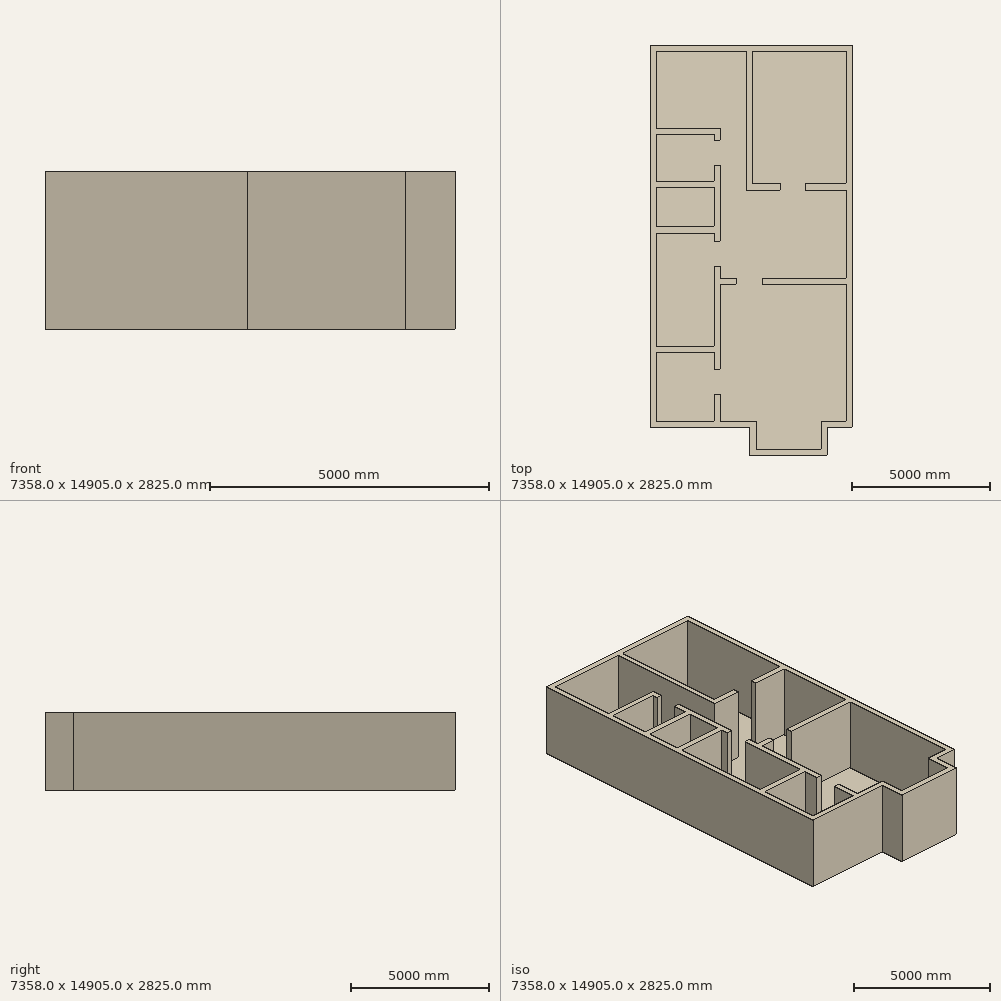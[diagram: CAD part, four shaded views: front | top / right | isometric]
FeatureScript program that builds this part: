
annotation { "Feature Type Name" : "Feature", "Feature Type Description" : "" }
export const myFeature = defineFeature(function(context is Context, id is Id, definition is map)
    precondition{}
    {
        {
            var Q0;
            Q0=qCreatedBy(makeId("Top.planeOp"),FACE);
            var sketch = newSketch(context, id + "F0", { "sketchPlane" : qUnion([Q0])});
            skLineSegment(sketch, "E0.bottom", {"start": v(0, 0) * mm, "end": v(2089, 0) * mm});
            skLineSegment(sketch, "E0.top", {"start": v(0, 13440) * mm, "end": v(3275, 13440) * mm});
            skLineSegment(sketch, "E0.left", {"start": v(0, 0) * mm, "end": v(0, 1938.71) * mm});
            skLineSegment(sketch, "E0.right", {"start": v(6900, 0) * mm, "end": v(6900, 4974) * mm});
            skLineSegment(sketch, "E1.0", {"start": v(7129, -229) * mm, "end": v(7129, 13669) * mm});
            skLineSegment(sketch, "E1.1", {"start": v(-229, -229) * mm, "end": v(3391, -229) * mm});
            skLineSegment(sketch, "E1.2", {"start": v(-229, -229) * mm, "end": v(-229, 13669) * mm});
            skLineSegment(sketch, "E1.3", {"start": v(-229, 13669) * mm, "end": v(7129, 13669) * mm});
            skLineSegment(sketch, "E2", {"start": v(6900, 4974) * mm, "end": v(3832.25, 4974) * mm});
            skLineSegment(sketch, "E3", {"start": v(3832.25, 4974) * mm, "end": v(3832.25, 5203) * mm});
            skLineSegment(sketch, "E4", {"start": v(3832.25, 5203) * mm, "end": v(6900, 5203) * mm});
            skLineSegment(sketch, "E5.trimOffspring", {"start": v(6900, 5203) * mm, "end": v(6900, 13440) * mm});
            skLineSegment(sketch, "E6", {"start": v(2318, 1893.08) * mm, "end": v(2318, 5631) * mm});
            skLineSegment(sketch, "E7", {"start": v(0, 0) * mm, "end": v(0, 2512) * mm});
            skLineSegment(sketch, "E8", {"start": v(0, 10652) * mm, "end": v(2318, 10652) * mm});
            skLineSegment(sketch, "E9", {"start": v(2089, 10423) * mm, "end": v(0, 10423) * mm});
            skLineSegment(sketch, "E10", {"start": v(0, 8735) * mm, "end": v(2089, 8735) * mm});
            skLineSegment(sketch, "E11", {"start": v(0, 8506) * mm, "end": v(2089, 8506) * mm});
            skLineSegment(sketch, "E12", {"start": v(0, 7080) * mm, "end": v(2089, 7080) * mm});
            skLineSegment(sketch, "E13", {"start": v(0, 6851) * mm, "end": v(2089, 6851) * mm});
            skLineSegment(sketch, "E14", {"start": v(0, 2741) * mm, "end": v(2089, 2741) * mm});
            skLineSegment(sketch, "E15", {"start": v(0, 2512) * mm, "end": v(2089, 2512) * mm});
            skLineSegment(sketch, "E16", {"start": v(2318, 1893.08) * mm, "end": v(2089, 1893.08) * mm});
            skLineSegment(sketch, "E17", {"start": v(2089, 1893.08) * mm, "end": v(2089, 2512) * mm});
            skLineSegment(sketch, "E18.trimOffspring", {"start": v(0, 2741) * mm, "end": v(0, 6851) * mm});
            skLineSegment(sketch, "E19.trimOffspring", {"start": v(2089, 2741) * mm, "end": v(2089, 5631) * mm});
            skLineSegment(sketch, "E20.trimOffspring", {"start": v(2089, 7080) * mm, "end": v(2089, 8506) * mm});
            skLineSegment(sketch, "E21.trimOffspring", {"start": v(0, 7080) * mm, "end": v(0, 8506) * mm});
            skLineSegment(sketch, "E22.trimOffspring", {"start": v(2089, 8735) * mm, "end": v(2089, 9303) * mm});
            skLineSegment(sketch, "E23.trimOffspring", {"start": v(0, 8735) * mm, "end": v(0, 13440) * mm});
            skLineSegment(sketch, "E24", {"start": v(2089, 973.08) * mm, "end": v(2089, 0) * mm});
            skLineSegment(sketch, "E25", {"start": v(2089, 973.08) * mm, "end": v(2318, 973.08) * mm});
            skLineSegment(sketch, "E26", {"start": v(2318, 973.08) * mm, "end": v(2318, 0) * mm});
            skLineSegment(sketch, "E27.trimOffspring", {"start": v(2318, 0) * mm, "end": v(3620, 0) * mm});
            skLineSegment(sketch, "E28", {"start": v(2318, 5203) * mm, "end": v(2912.25, 5203) * mm});
            skLineSegment(sketch, "E29", {"start": v(2912.25, 5203) * mm, "end": v(2912.25, 4974) * mm});
            skLineSegment(sketch, "E30", {"start": v(2912.25, 4974) * mm, "end": v(2318, 4974) * mm});
            skLineSegment(sketch, "E31", {"start": v(2089, 6551) * mm, "end": v(2318, 6551) * mm});
            skLineSegment(sketch, "E32", {"start": v(2089, 5631) * mm, "end": v(2318, 5631) * mm});
            skLineSegment(sketch, "E33.trimOffspring", {"start": v(2089, 6551) * mm, "end": v(2089, 6851) * mm});
            skLineSegment(sketch, "E34.trimOffspring", {"start": v(2318, 6551) * mm, "end": v(2318, 9303) * mm});
            skLineSegment(sketch, "E35", {"start": v(2089, 10223) * mm, "end": v(2318, 10223) * mm});
            skLineSegment(sketch, "E36", {"start": v(2089, 9303) * mm, "end": v(2318, 9303) * mm});
            skLineSegment(sketch, "E37.trimOffspring", {"start": v(2318, 10223) * mm, "end": v(2318, 10652) * mm});
            skLineSegment(sketch, "E38.trimOffspring", {"start": v(2089, 10223) * mm, "end": v(2089, 10423) * mm});
            skPoint(sketch, "E39.endSnap0", {"position": v(3450, 13440) * mm});
            skLineSegment(sketch, "E40", {"start": v(6900, 8638) * mm, "end": v(5416.42, 8638) * mm});
            skLineSegment(sketch, "E41", {"start": v(5416.42, 8638) * mm, "end": v(5416.42, 8409) * mm});
            skLineSegment(sketch, "E42", {"start": v(5416.42, 8409) * mm, "end": v(6900, 8409) * mm});
            skLineSegment(sketch, "E43", {"start": v(3504, 13440) * mm, "end": v(3504, 8638) * mm});
            skLineSegment(sketch, "E44", {"start": v(3275, 13440) * mm, "end": v(3275, 8409) * mm});
            skLineSegment(sketch, "E45", {"start": v(3275, 8409) * mm, "end": v(4496.42, 8409) * mm});
            skLineSegment(sketch, "E46", {"start": v(4496.42, 8409) * mm, "end": v(4496.42, 8638) * mm});
            skLineSegment(sketch, "E47", {"start": v(4496.42, 8638) * mm, "end": v(3504, 8638) * mm});
            skLineSegment(sketch, "E48.trimOffspring", {"start": v(3504, 13440) * mm, "end": v(6900, 13440) * mm});
            skLineSegment(sketch, "E49", {"start": v(6229, -229) * mm, "end": v(6229, -1236) * mm});
            skLineSegment(sketch, "E50", {"start": v(6229, -1236) * mm, "end": v(3391, -1236) * mm});
            skLineSegment(sketch, "E51", {"start": v(3391, -1236) * mm, "end": v(3391, -229) * mm});
            skLineSegment(sketch, "E52", {"start": v(3620, 0) * mm, "end": v(3620, -1007) * mm});
            skLineSegment(sketch, "E53", {"start": v(3620, -1007) * mm, "end": v(6000, -1007) * mm});
            skLineSegment(sketch, "E54", {"start": v(6000, -1007) * mm, "end": v(6000, 0) * mm});
            skLineSegment(sketch, "E55.trimOffspring", {"start": v(6000, 0) * mm, "end": v(6900, 0) * mm});
            skLineSegment(sketch, "E56.trimOffspring", {"start": v(6229, -229) * mm, "end": v(7129, -229) * mm});
            skSolve(sketch);
        }
        {
            var Q0;
            {var subQ8=sQuery(id+"F0.wireOp",EDGE,"E0.bottom");Q0=makeQuery(id+"F0.imprint","IMPRINT",FACE,{"disambiguationData":[TD([[makeQuery(id+"F0.imprint","IMPRINT",EDGE,{"derivedFrom":subQ8}),-1.0]])]});}
            var Q1;
            {var subQ0=sQuery(id+"F0.wireOp",EDGE,"E40");Q1=makeQuery(id+"F0.imprint","IMPRINT",FACE,{"disambiguationData":[TD([[makeQuery(id+"F0.imprint","IMPRINT",EDGE,{"derivedFrom":subQ0}),1.0]])]});}
            var Q2;
            {var subQ1=sQuery(id+"F0.wireOp",EDGE,"E8");Q2=makeQuery(id+"F0.imprint","IMPRINT",FACE,{"disambiguationData":[TD([[makeQuery(id+"F0.imprint","IMPRINT",EDGE,{"derivedFrom":subQ1}),-1.0]])]});}
            var Q3;
            {var subQ0=sQuery(id+"F0.wireOp",EDGE,"E28");Q3=makeQuery(id+"F0.imprint","IMPRINT",FACE,{"disambiguationData":[TD([[makeQuery(id+"F0.imprint","IMPRINT",EDGE,{"derivedFrom":subQ0}),-1.0]])]});}
            extrude(context, id + "F1", {"entities" : qUnion([Q0, Q1, Q2, Q3]), "depth" : 2800 * mm});
        }
        {
            var Q0;
            Q0=makeQuery(id+"F1.opExtrude","CAP_FACE",FACE,{"disambiguationData":[OSD([sQuery(id+"F0.wireOp",EDGE,"E0.bottom"),sQuery(id+"F0.wireOp",EDGE,"E0.top"),sQuery(id+"F0.wireOp",EDGE,"E0.right"),sQuery(id+"F0.wireOp",EDGE,"E1.0"),sQuery(id+"F0.wireOp",EDGE,"E1.1"),sQuery(id+"F0.wireOp",EDGE,"E1.2"),sQuery(id+"F0.wireOp",EDGE,"E1.3"),sQuery(id+"F0.wireOp",EDGE,"E2"),sQuery(id+"F0.wireOp",EDGE,"E3"),sQuery(id+"F0.wireOp",EDGE,"E4"),sQuery(id+"F0.wireOp",EDGE,"E5.trimOffspring"),sQuery(id+"F0.wireOp",EDGE,"E6"),sQuery(id+"F0.wireOp",EDGE,"E7"),sQuery(id+"F0.wireOp",EDGE,"E8"),sQuery(id+"F0.wireOp",EDGE,"E9"),sQuery(id+"F0.wireOp",EDGE,"E10"),sQuery(id+"F0.wireOp",EDGE,"E11"),sQuery(id+"F0.wireOp",EDGE,"E12"),sQuery(id+"F0.wireOp",EDGE,"E13"),sQuery(id+"F0.wireOp",EDGE,"E14"),sQuery(id+"F0.wireOp",EDGE,"E15"),sQuery(id+"F0.wireOp",EDGE,"E16"),sQuery(id+"F0.wireOp",EDGE,"E17"),sQuery(id+"F0.wireOp",EDGE,"E18.trimOffspring"),sQuery(id+"F0.wireOp",EDGE,"E19.trimOffspring"),sQuery(id+"F0.wireOp",EDGE,"E20.trimOffspring"),sQuery(id+"F0.wireOp",EDGE,"E21.trimOffspring"),sQuery(id+"F0.wireOp",EDGE,"E22.trimOffspring"),sQuery(id+"F0.wireOp",EDGE,"E23.trimOffspring"),sQuery(id+"F0.wireOp",EDGE,"E24"),sQuery(id+"F0.wireOp",EDGE,"E25"),sQuery(id+"F0.wireOp",EDGE,"E26"),sQuery(id+"F0.wireOp",EDGE,"E27.trimOffspring"),sQuery(id+"F0.wireOp",EDGE,"E28"),sQuery(id+"F0.wireOp",EDGE,"E29"),sQuery(id+"F0.wireOp",EDGE,"E30"),sQuery(id+"F0.wireOp",EDGE,"E31"),sQuery(id+"F0.wireOp",EDGE,"E32"),sQuery(id+"F0.wireOp",EDGE,"E33.trimOffspring"),sQuery(id+"F0.wireOp",EDGE,"E34.trimOffspring"),sQuery(id+"F0.wireOp",EDGE,"E35"),sQuery(id+"F0.wireOp",EDGE,"E36"),sQuery(id+"F0.wireOp",EDGE,"E37.trimOffspring"),sQuery(id+"F0.wireOp",EDGE,"E38.trimOffspring"),sQuery(id+"F0.wireOp",EDGE,"E40"),sQuery(id+"F0.wireOp",EDGE,"E41"),sQuery(id+"F0.wireOp",EDGE,"E42"),sQuery(id+"F0.wireOp",EDGE,"E43"),sQuery(id+"F0.wireOp",EDGE,"E44"),sQuery(id+"F0.wireOp",EDGE,"E45"),sQuery(id+"F0.wireOp",EDGE,"E46"),sQuery(id+"F0.wireOp",EDGE,"E47"),sQuery(id+"F0.wireOp",EDGE,"E48.trimOffspring"),sQuery(id+"F0.wireOp",EDGE,"E49"),sQuery(id+"F0.wireOp",EDGE,"E50"),sQuery(id+"F0.wireOp",EDGE,"E51"),sQuery(id+"F0.wireOp",EDGE,"E52"),sQuery(id+"F0.wireOp",EDGE,"E53"),sQuery(id+"F0.wireOp",EDGE,"E54"),sQuery(id+"F0.wireOp",EDGE,"E55.trimOffspring"),sQuery(id+"F0.wireOp",EDGE,"E56.trimOffspring")])],"isStart":true});
            var sketch = newSketch(context, id + "F2", { "sketchPlane" : qUnion([Q0])});
            skLineSegment(sketch, "E57", {"start": v(3391, 1236) * mm, "end": v(6229, 1236) * mm});
            skLineSegment(sketch, "E58", {"start": v(6229, 1236) * mm, "end": v(6229, 229) * mm});
            skLineSegment(sketch, "E59", {"start": v(6229, 229) * mm, "end": v(7129, 229) * mm});
            skLineSegment(sketch, "E60", {"start": v(7129, 229) * mm, "end": v(7129, -13669) * mm});
            skLineSegment(sketch, "E61", {"start": v(7129, -13669) * mm, "end": v(-229, -13669) * mm});
            skLineSegment(sketch, "E62", {"start": v(-229, -13669) * mm, "end": v(-229, 229) * mm});
            skLineSegment(sketch, "E63", {"start": v(-229, 229) * mm, "end": v(3391, 229) * mm});
            skLineSegment(sketch, "E64", {"start": v(3391, 229) * mm, "end": v(3391, 1236) * mm});
            skSolve(sketch);
        }
        {
            var Q0;
            Q0 = qSketchRegion(id + "F2", true);
            extrude(context, id + "F3", {"entities" : qUnion([Q0]), "operationType" : NewBodyOperationType.ADD, "depth" : 25 * mm});
        }
    });
